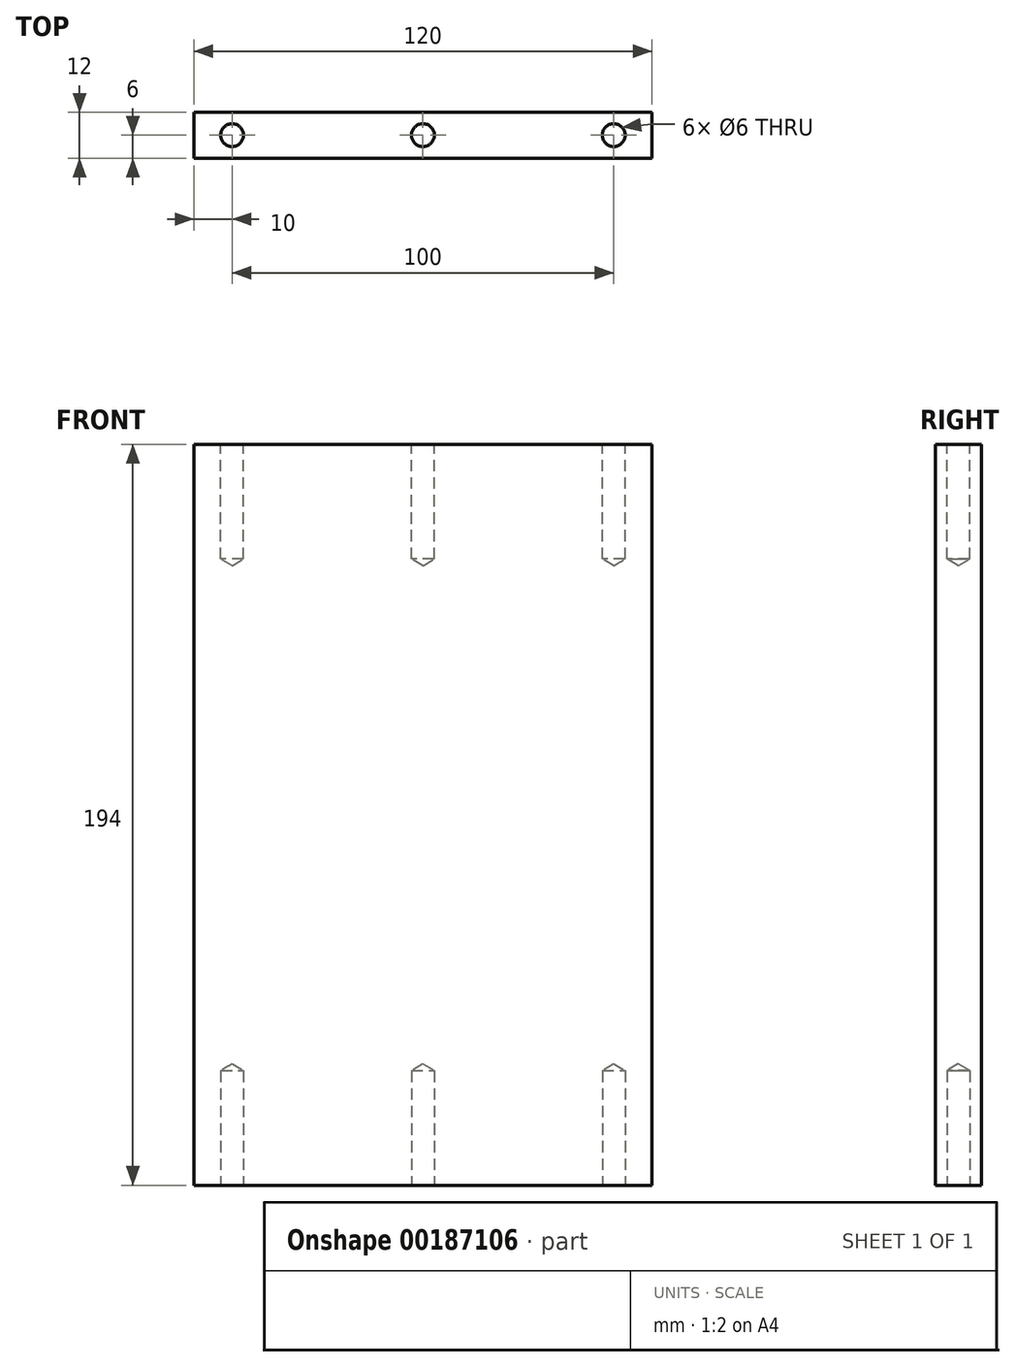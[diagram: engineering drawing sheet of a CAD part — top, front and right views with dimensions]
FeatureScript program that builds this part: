
annotation { "Feature Type Name" : "Feature", "Feature Type Description" : "" }
export const myFeature = defineFeature(function(context is Context, id is Id, definition is map)
    precondition{}
    {
        {
            var Q0;
            Q0=qCreatedBy(makeId("Front.planeOp"),FACE);
            var sketch = newSketch(context, id + "F0", { "sketchPlane" : qUnion([Q0])});
            skLineSegment(sketch, "E0.bottom", {"start": v(60, -97) * mm, "end": v(-60, -97) * mm});
            skLineSegment(sketch, "E0.top", {"start": v(60, 97) * mm, "end": v(-60, 97) * mm});
            skLineSegment(sketch, "E0.left", {"start": v(60, -97) * mm, "end": v(60, 97) * mm});
            skLineSegment(sketch, "E0.right", {"start": v(-60, -97) * mm, "end": v(-60, 97) * mm});
            skPoint(sketch, "E0.middle", {"position": v(0, 0) * mm});
            skSolve(sketch);
        }
        {
            var Q0;
            Q0=makeQuery(id+"F0.imprint","IMPRINT",FACE,{"disambiguationData":[TD([[makeQuery(id+"F0.imprint","IMPRINT",EDGE,{"derivedFrom":sQuery(id+"F0.wireOp",EDGE,"E0.bottom")}),-1.0]])]});
            extrude(context, id + "F1", {"entities" : qUnion([Q0]), "depth" : 12 * mm});
        }
        {
            var Q0;
            Q0=makeQuery(id+"F1.opExtrude","SWEPT_FACE",FACE,{"disambiguationData":[OSD([sQuery(id+"F0.wireOp",EDGE,"E0.top")])]});
            var sketch = newSketch(context, id + "F2", { "sketchPlane" : qUnion([Q0])});
            skCircle(sketch, "E1", {"center": v(-50, -6) * mm, "radius": 3 * mm});
            skCircle(sketch, "E2", {"center": v(0, -6) * mm, "radius": 3 * mm});
            skCircle(sketch, "E3", {"center": v(50, -6) * mm, "radius": 3 * mm});
            skSolve(sketch);
        }
        {
            var Q0;
            Q0=sQuery(id+"F2.wireOp",VERTEX,"E1.center");
            var Q1;
            Q1=sQuery(id+"F2.wireOp",VERTEX,"E2.center");
            var Q2;
            Q2=sQuery(id+"F2.wireOp",VERTEX,"E3.center");
            var Q3;
            Q3=makeQuery(id+"F1.opExtrude","SWEPT_BODY",BODY,{"disambiguationData":[OSD([sQuery(id+"F0.wireOp",EDGE,"E0.bottom"),sQuery(id+"F0.wireOp",EDGE,"E0.top"),sQuery(id+"F0.wireOp",EDGE,"E0.left"),sQuery(id+"F0.wireOp",EDGE,"E0.right")])]});
            hole(context, id + "F3", {"style" : HoleStyle.SIMPLE, "endStyle" : HoleEndStyle.BLIND, "holeDiameter" : 6 * mm, "holeDepth" : 30 * mm, "locations" : qUnion([Q0, Q1, Q2]), "scope" : qUnion([Q3])});
        }
        {
            var Q0;
            Q0=makeQuery(id+"F1.opExtrude","SWEPT_FACE",FACE,{"disambiguationData":[OSD([sQuery(id+"F0.wireOp",EDGE,"E0.bottom")])]});
            var sketch = newSketch(context, id + "F4", { "sketchPlane" : qUnion([Q0])});
            skCircle(sketch, "E4", {"center": v(-50, 6) * mm, "radius": 3 * mm});
            skCircle(sketch, "E5", {"center": v(0, 6) * mm, "radius": 3 * mm});
            skCircle(sketch, "E6", {"center": v(50, 6) * mm, "radius": 3 * mm});
            skSolve(sketch);
        }
        {
            var Q0;
            Q0=sQuery(id+"F4.wireOp",VERTEX,"E4.center");
            var Q1;
            Q1=sQuery(id+"F4.wireOp",VERTEX,"E5.center");
            var Q2;
            Q2=sQuery(id+"F4.wireOp",VERTEX,"E6.center");
            var Q3;
            Q3=makeQuery(id+"F1.opExtrude","SWEPT_BODY",BODY,{"disambiguationData":[OSD([sQuery(id+"F0.wireOp",EDGE,"E0.bottom"),sQuery(id+"F0.wireOp",EDGE,"E0.top"),sQuery(id+"F0.wireOp",EDGE,"E0.left"),sQuery(id+"F0.wireOp",EDGE,"E0.right")])]});
            hole(context, id + "F5", {"style" : HoleStyle.SIMPLE, "endStyle" : HoleEndStyle.BLIND, "holeDiameter" : 6 * mm, "holeDepth" : 30 * mm, "locations" : qUnion([Q0, Q1, Q2]), "scope" : qUnion([Q3])});
        }
    });
